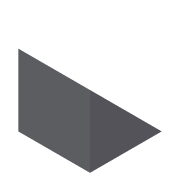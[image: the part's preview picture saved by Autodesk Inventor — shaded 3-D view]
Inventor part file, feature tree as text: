
AUTODESK INVENTOR PART (.ipt)
format: ipt  version: 2015 (Build 190159000, 159)  size: 70,656 bytes
history: native  units: mm
features: extrude x1, chamfer x1, sketch x1
ambient origin geometry x8: Origin, YZ Plane, XZ Plane, XY Plane, X Axis, Y Axis, Z Axis, Center Point
bodies: Solid1 (feature_tree)
feature tree (3):
  extrude  "Extrusion1"  Depth=30.0mm
  chamfer  "Chamfer1"  Distance=30.0mm
  sketch  "Sketch1"  dims[d0=30.0mm d1=30.0mm d2=30.0mm d3=0.0mm d4=30.0mm d5=2.0mm d6=45.0deg]
